# Revit family: Verano_V909_Somerset_GM_R21
name_source: partatom
category: Generic Models
units: mm (PartAtom-declared; Revit-internal decimal feet)

## family parameters
Always vertical = Yes
Can host rebar = No
Cut with Voids When Loaded = No
Part Type = Normal
Room Calculation Point = No
Round Connector Dimension = Use Diameter
Shared = No
Work Plane-Based = No

## types (3) — shared parameters
Manufacturer = Verano Systems
Maximal Angle = 45.00°
Maximal H1 = 5596 mm
Maximal Pillar Height = 2500 mm  [stored 8.2021 ft]
Maximal Projection = 3000 mm  [stored 9.84252 ft]
Maximal Width = 14000 mm
Minimal Angle = 5.00°
Minimal Projection = 2000 mm  [stored 6.56168 ft]
Minimal Width = 3000 mm  [stored 9.84252 ft]
Model = V909 Somerset
URL = https://verano.nl
zero-valued in all types: Default Elevation

## per-type parameters (varying)
| type | Column Type 1 | Column Type 2 | Column Type 3 |
| Post A | Yes | No | No |
| Post B | No | Yes | No |
| Post C | No | No | Yes |

note: [stored X ft] marks values corroborated as IEEE doubles in the binary element streams (Revit-internal decimal feet)

## geometry (parser evidence)
native form markers: Extrusion x2, Sweep x42
no freeform markers — native parametric forms only
